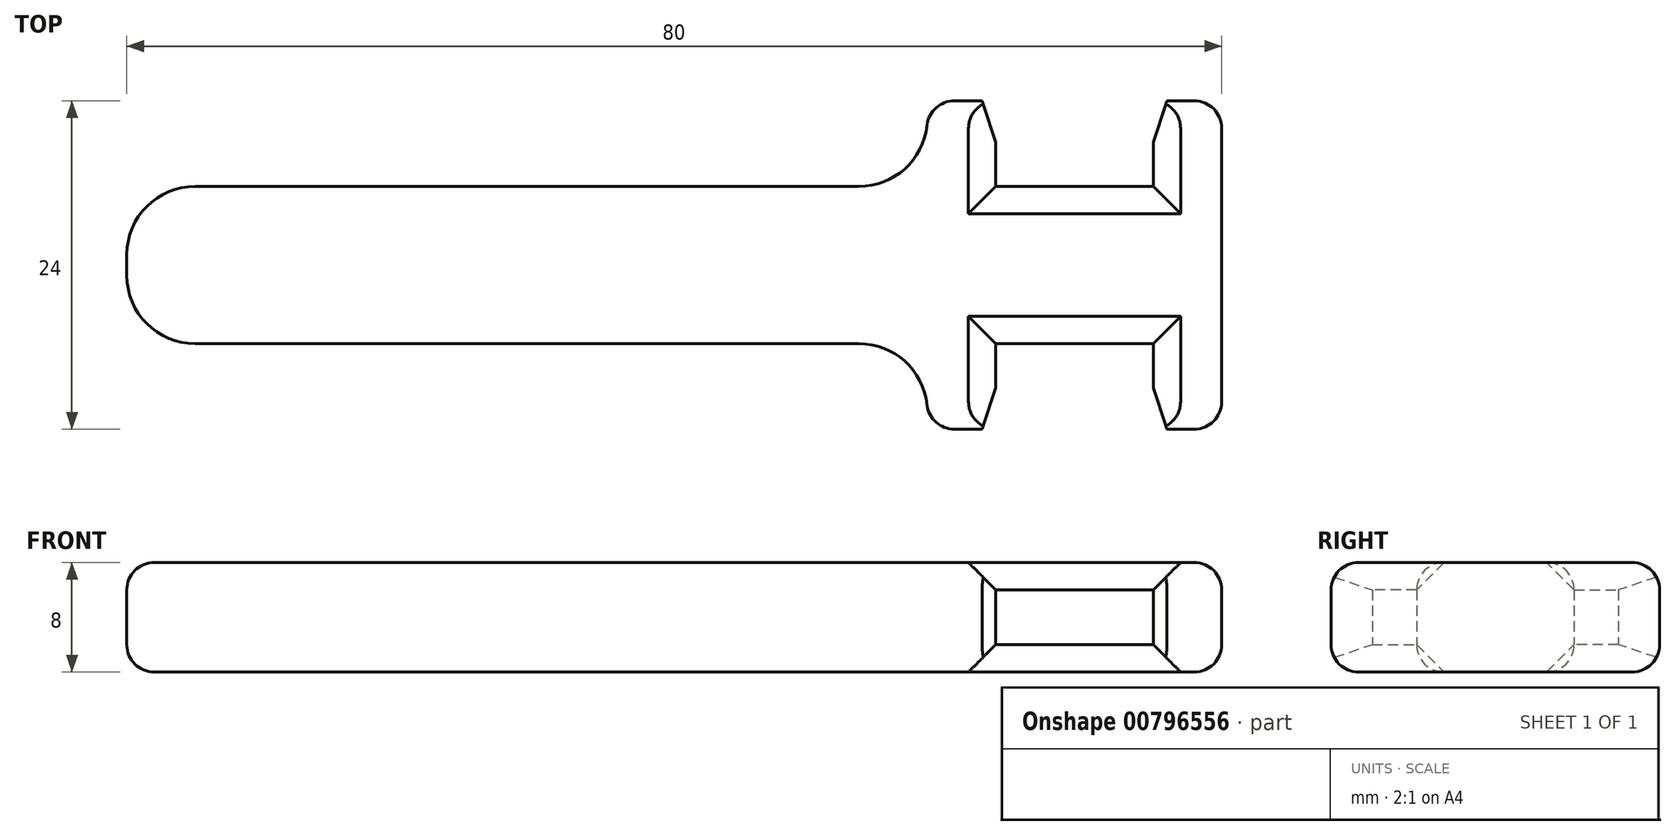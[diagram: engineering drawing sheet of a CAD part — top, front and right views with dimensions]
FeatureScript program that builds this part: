
annotation { "Feature Type Name" : "Feature", "Feature Type Description" : "" }
export const myFeature = defineFeature(function(context is Context, id is Id, definition is map)
    precondition{}
    {
        {
            var Q0;
            Q0=qCreatedBy(makeId("Top.planeOp"),FACE);
            var sketch = newSketch(context, id + "F0", { "sketchPlane" : qUnion([Q0])});
            skLineSegment(sketch, "E0.bottom", {"start": v(35, -5.75) * mm, "end": v(23.5, -5.75) * mm});
            skLineSegment(sketch, "E0.top", {"start": v(35, 5.75) * mm, "end": v(23.5, 5.75) * mm});
            skLineSegment(sketch, "E0.left", {"start": v(40, -5.75) * mm, "end": v(40, 5.75) * mm});
            skLineSegment(sketch, "E0.right", {"start": v(-40, -5.75) * mm, "end": v(-40, 5.75) * mm});
            skPoint(sketch, "E0.middle", {"position": v(0, 0) * mm});
            skLineSegment(sketch, "E1.bottom", {"start": v(40, 12) * mm, "end": v(35, 12) * mm});
            skLineSegment(sketch, "E1.top", {"start": v(40, -12) * mm, "end": v(35, -12) * mm});
            skLineSegment(sketch, "E1.left", {"start": v(40, 12) * mm, "end": v(40, -12) * mm});
            skLineSegment(sketch, "E1.right", {"start": v(35, 12) * mm, "end": v(35, 5.75) * mm});
            skLineSegment(sketch, "E2.trimOffspring", {"start": v(35, -5.75) * mm, "end": v(35, -12) * mm});
            skLineSegment(sketch, "E3.bottom", {"start": v(18.5, -12) * mm, "end": v(23.5, -12) * mm});
            skLineSegment(sketch, "E3.top", {"start": v(18.5, 12) * mm, "end": v(23.5, 12) * mm});
            skLineSegment(sketch, "E3.left", {"start": v(18.5, -12) * mm, "end": v(18.5, -5.75) * mm});
            skLineSegment(sketch, "E3.right", {"start": v(23.5, -12) * mm, "end": v(23.5, -5.75) * mm});
            skPoint(sketch, "E3.middle", {"position": v(21, 0) * mm});
            skLineSegment(sketch, "E4.trimOffspring", {"start": v(23.5, 5.75) * mm, "end": v(23.5, 12) * mm});
            skLineSegment(sketch, "E5.trimOffspring", {"start": v(18.5, 5.75) * mm, "end": v(18.5, 12) * mm});
            skLineSegment(sketch, "E6.trimOffspring", {"start": v(18.5, 5.75) * mm, "end": v(-40, 5.75) * mm});
            skLineSegment(sketch, "E7.trimOffspring", {"start": v(18.5, -5.75) * mm, "end": v(-40, -5.75) * mm});
            skSolve(sketch);
        }
        {
            var Q0;
            Q0 = qSketchRegion(id + "F0", true);
            extrude(context, id + "F1", {"entities" : qUnion([Q0]), "depth" : 8 * mm, "offsetDistance" : 25 * mm});
        }
        {
            var Q0;
            Q0=makeQuery(id+"F1.opExtrude","SWEPT_EDGE",EDGE,{"disambiguationData":[OSD([sQuery(id+"F0.wireOp",EDGE,"E3.left"),sQuery(id+"F0.wireOp",EDGE,"E7.trimOffspring")])]});
            var Q1;
            Q1=makeQuery(id+"F1.opExtrude","SWEPT_EDGE",EDGE,{"disambiguationData":[OSD([sQuery(id+"F0.wireOp",EDGE,"E5.trimOffspring"),sQuery(id+"F0.wireOp",EDGE,"E6.trimOffspring")])]});
            var Q2;
            Q2=makeQuery(id+"F1.opExtrude","SWEPT_EDGE",EDGE,{"disambiguationData":[OSD([sQuery(id+"F0.wireOp",EDGE,"E0.right"),sQuery(id+"F0.wireOp",EDGE,"E7.trimOffspring")])]});
            var Q3;
            Q3=makeQuery(id+"F1.opExtrude","SWEPT_EDGE",EDGE,{"disambiguationData":[OSD([sQuery(id+"F0.wireOp",EDGE,"E0.right"),sQuery(id+"F0.wireOp",EDGE,"E6.trimOffspring")])]});
            fillet(context, id + "F2", {"entities" : qUnion([Q0, Q1, Q2, Q3]), "radius" : 5 * mm, "tangentPropagation" : true, "allowEdgeOverflow" : false});
        }
        {
            var Q0;
            Q0=makeQuery(id+"F1.opExtrude","SWEPT_EDGE",EDGE,{"disambiguationData":[OSD([sQuery(id+"F0.wireOp",EDGE,"E1.top"),sQuery(id+"F0.wireOp",EDGE,"E1.left")])]});
            var Q1;
            Q1=makeQuery(id+"F1.opExtrude","SWEPT_EDGE",EDGE,{"disambiguationData":[OSD([sQuery(id+"F0.wireOp",EDGE,"E1.bottom"),sQuery(id+"F0.wireOp",EDGE,"E1.left")])]});
            var Q2;
            Q2=makeQuery(id+"F1.opExtrude","SWEPT_EDGE",EDGE,{"disambiguationData":[OSD([sQuery(id+"F0.wireOp",EDGE,"E3.bottom"),sQuery(id+"F0.wireOp",EDGE,"E3.left")])]});
            var Q3;
            Q3=makeQuery(id+"F1.opExtrude","SWEPT_EDGE",EDGE,{"disambiguationData":[OSD([sQuery(id+"F0.wireOp",EDGE,"E3.top"),sQuery(id+"F0.wireOp",EDGE,"E5.trimOffspring")])]});
            fillet(context, id + "F3", {"entities" : qUnion([Q0, Q1, Q2, Q3]), "radius" : 2 * mm, "tangentPropagation" : true, "allowEdgeOverflow" : false});
        }
        {
            var Q0;
            Q0=makeQuery(id+"F1.opExtrude","SWEPT_EDGE",EDGE,{"disambiguationData":[OSD([sQuery(id+"F0.wireOp",EDGE,"E3.top"),sQuery(id+"F0.wireOp",EDGE,"E4.trimOffspring")])]});
            var Q1;
            Q1=makeQuery(id+"F1.opExtrude","SWEPT_EDGE",EDGE,{"disambiguationData":[OSD([sQuery(id+"F0.wireOp",EDGE,"E1.top"),sQuery(id+"F0.wireOp",EDGE,"E2.trimOffspring")])]});
            chamfer(context, id + "F4", {"entities" : qUnion([Q0, Q1]), "chamferType" : ChamferType.TWO_OFFSETS, "width1" : 1 * mm, "oppositeDirection" : false, "width2" : 3 * mm, "tangentPropagation" : true});
        }
        {
            var Q0;
            Q0=makeQuery(id+"F1.opExtrude","SWEPT_EDGE",EDGE,{"disambiguationData":[OSD([sQuery(id+"F0.wireOp",EDGE,"E3.bottom"),sQuery(id+"F0.wireOp",EDGE,"E3.right")])]});
            var Q1;
            Q1=makeQuery(id+"F1.opExtrude","SWEPT_EDGE",EDGE,{"disambiguationData":[OSD([sQuery(id+"F0.wireOp",EDGE,"E1.bottom"),sQuery(id+"F0.wireOp",EDGE,"E1.right")])]});
            chamfer(context, id + "F5", {"entities" : qUnion([Q0, Q1]), "chamferType" : ChamferType.TWO_OFFSETS, "width1" : 3 * mm, "oppositeDirection" : false, "width2" : 1 * mm, "tangentPropagation" : true});
        }
        {
            var Q0;
            Q0=makeQuery(id+"F1.opExtrude","CAP_EDGE",EDGE,{"disambiguationData":[OSD([sQuery(id+"F0.wireOp",EDGE,"E0.top")])],"isStart":false});
            var Q1;
            Q1=makeQuery(id+"F1.opExtrude","CAP_EDGE",EDGE,{"disambiguationData":[OSD([sQuery(id+"F0.wireOp",EDGE,"E0.bottom")])],"isStart":false});
            var Q2;
            Q2=makeQuery(id+"F1.opExtrude","CAP_EDGE",EDGE,{"disambiguationData":[OSD([sQuery(id+"F0.wireOp",EDGE,"E0.bottom")])],"isStart":true});
            var Q3;
            Q3=makeQuery(id+"F1.opExtrude","CAP_EDGE",EDGE,{"disambiguationData":[OSD([sQuery(id+"F0.wireOp",EDGE,"E0.top")])],"isStart":true});
            var Q4;
            Q4=makeQuery(id+"F1.opExtrude","CAP_EDGE",EDGE,{"disambiguationData":[OSD([sQuery(id+"F0.wireOp",EDGE,"E4.trimOffspring")])],"isStart":true});
            var Q5;
            Q5=makeQuery(id+"F1.opExtrude","CAP_EDGE",EDGE,{"disambiguationData":[OSD([sQuery(id+"F0.wireOp",EDGE,"E4.trimOffspring")])],"isStart":false});
            var Q6;
            Q6=makeQuery(id+"F1.opExtrude","CAP_EDGE",EDGE,{"disambiguationData":[OSD([sQuery(id+"F0.wireOp",EDGE,"E3.right")])],"isStart":false});
            var Q7;
            Q7=makeQuery(id+"F1.opExtrude","CAP_EDGE",EDGE,{"disambiguationData":[OSD([sQuery(id+"F0.wireOp",EDGE,"E3.right")])],"isStart":true});
            var Q8;
            Q8=makeQuery(id+"F1.opExtrude","CAP_EDGE",EDGE,{"disambiguationData":[OSD([sQuery(id+"F0.wireOp",EDGE,"E2.trimOffspring")])],"isStart":true});
            var Q9;
            Q9=makeQuery(id+"F1.opExtrude","CAP_EDGE",EDGE,{"disambiguationData":[OSD([sQuery(id+"F0.wireOp",EDGE,"E2.trimOffspring")])],"isStart":false});
            var Q10;
            Q10=makeQuery(id+"F1.opExtrude","CAP_EDGE",EDGE,{"disambiguationData":[OSD([sQuery(id+"F0.wireOp",EDGE,"E1.right")])],"isStart":true});
            var Q11;
            Q11=makeQuery(id+"F1.opExtrude","CAP_EDGE",EDGE,{"disambiguationData":[OSD([sQuery(id+"F0.wireOp",EDGE,"E1.right")])],"isStart":false});
            chamfer(context, id + "F6", {"entities" : qUnion([Q0, Q1, Q2, Q3, Q4, Q5, Q6, Q7, Q8, Q9, Q10, Q11]), "width" : 2 * mm, "tangentPropagation" : true});
        }
        {
            var Q0;
            Q0=makeQuery(id+"F1.opExtrude","CAP_EDGE",EDGE,{"disambiguationData":[OSD([sQuery(id+"F0.wireOp",EDGE,"E7.trimOffspring")])],"isStart":true});
            fillet(context, id + "F7", {"entities" : qUnion([Q0]), "radius" : 2 * mm, "tangentPropagation" : true, "allowEdgeOverflow" : false});
        }
        {
            var Q0;
            Q0=makeQuery(id+"F1.opExtrude","CAP_EDGE",EDGE,{"disambiguationData":[OSD([sQuery(id+"F0.wireOp",EDGE,"E7.trimOffspring")])],"isStart":false});
            var Q1;
            {var subQ0=sQuery(id+"F0.wireOp",EDGE,"E7.trimOffspring");var subQ1=sQuery(id+"F0.wireOp",EDGE,"E3.left");Q1=makeQuery(id+"F2.opFillet","BLEND_EDGE",EDGE,{"blendedFrom":[makeQuery(id+"F1.opExtrude","SWEPT_EDGE",EDGE,{"disambiguationData":[OSD([subQ1,subQ0])]}),makeQuery(id+"F1.opExtrude","CAP_FACE",FACE,{"disambiguationData":[OSD([sQuery(id+"F0.wireOp",EDGE,"E0.bottom"),sQuery(id+"F0.wireOp",EDGE,"E0.top"),sQuery(id+"F0.wireOp",EDGE,"E0.right"),sQuery(id+"F0.wireOp",EDGE,"E1.bottom"),sQuery(id+"F0.wireOp",EDGE,"E1.top"),sQuery(id+"F0.wireOp",EDGE,"E1.left"),sQuery(id+"F0.wireOp",EDGE,"E1.right"),sQuery(id+"F0.wireOp",EDGE,"E2.trimOffspring"),sQuery(id+"F0.wireOp",EDGE,"E3.bottom"),sQuery(id+"F0.wireOp",EDGE,"E3.top"),subQ1,sQuery(id+"F0.wireOp",EDGE,"E3.right"),sQuery(id+"F0.wireOp",EDGE,"E4.trimOffspring"),sQuery(id+"F0.wireOp",EDGE,"E5.trimOffspring"),sQuery(id+"F0.wireOp",EDGE,"E6.trimOffspring"),subQ0])],"isStart":false})],"blendedInto":[makeQuery(id+"F1.opExtrude","CAP_FACE",FACE,{"disambiguationData":[OSD([sQuery(id+"F0.wireOp",EDGE,"E0.bottom"),sQuery(id+"F0.wireOp",EDGE,"E0.top"),sQuery(id+"F0.wireOp",EDGE,"E0.right"),sQuery(id+"F0.wireOp",EDGE,"E1.bottom"),sQuery(id+"F0.wireOp",EDGE,"E1.top"),sQuery(id+"F0.wireOp",EDGE,"E1.left"),sQuery(id+"F0.wireOp",EDGE,"E1.right"),sQuery(id+"F0.wireOp",EDGE,"E2.trimOffspring"),sQuery(id+"F0.wireOp",EDGE,"E3.bottom"),sQuery(id+"F0.wireOp",EDGE,"E3.top"),subQ1,sQuery(id+"F0.wireOp",EDGE,"E3.right"),sQuery(id+"F0.wireOp",EDGE,"E4.trimOffspring"),sQuery(id+"F0.wireOp",EDGE,"E5.trimOffspring"),sQuery(id+"F0.wireOp",EDGE,"E6.trimOffspring"),subQ0])],"isStart":false})]});}
            var Q2;
            Q2=makeQuery(id+"F1.opExtrude","CAP_EDGE",EDGE,{"disambiguationData":[OSD([sQuery(id+"F0.wireOp",EDGE,"E6.trimOffspring")])],"isStart":false});
            var Q3;
            {var subQ0=sQuery(id+"F0.wireOp",EDGE,"E6.trimOffspring");var subQ1=sQuery(id+"F0.wireOp",EDGE,"E5.trimOffspring");Q3=makeQuery(id+"F2.opFillet","BLEND_EDGE",EDGE,{"blendedFrom":[makeQuery(id+"F1.opExtrude","SWEPT_EDGE",EDGE,{"disambiguationData":[OSD([subQ1,subQ0])]}),makeQuery(id+"F1.opExtrude","CAP_FACE",FACE,{"disambiguationData":[OSD([sQuery(id+"F0.wireOp",EDGE,"E0.bottom"),sQuery(id+"F0.wireOp",EDGE,"E0.top"),sQuery(id+"F0.wireOp",EDGE,"E0.right"),sQuery(id+"F0.wireOp",EDGE,"E1.bottom"),sQuery(id+"F0.wireOp",EDGE,"E1.top"),sQuery(id+"F0.wireOp",EDGE,"E1.left"),sQuery(id+"F0.wireOp",EDGE,"E1.right"),sQuery(id+"F0.wireOp",EDGE,"E2.trimOffspring"),sQuery(id+"F0.wireOp",EDGE,"E3.bottom"),sQuery(id+"F0.wireOp",EDGE,"E3.top"),sQuery(id+"F0.wireOp",EDGE,"E3.left"),sQuery(id+"F0.wireOp",EDGE,"E3.right"),sQuery(id+"F0.wireOp",EDGE,"E4.trimOffspring"),subQ1,subQ0,sQuery(id+"F0.wireOp",EDGE,"E7.trimOffspring")])],"isStart":false})],"blendedInto":[makeQuery(id+"F1.opExtrude","CAP_FACE",FACE,{"disambiguationData":[OSD([sQuery(id+"F0.wireOp",EDGE,"E0.bottom"),sQuery(id+"F0.wireOp",EDGE,"E0.top"),sQuery(id+"F0.wireOp",EDGE,"E0.right"),sQuery(id+"F0.wireOp",EDGE,"E1.bottom"),sQuery(id+"F0.wireOp",EDGE,"E1.top"),sQuery(id+"F0.wireOp",EDGE,"E1.left"),sQuery(id+"F0.wireOp",EDGE,"E1.right"),sQuery(id+"F0.wireOp",EDGE,"E2.trimOffspring"),sQuery(id+"F0.wireOp",EDGE,"E3.bottom"),sQuery(id+"F0.wireOp",EDGE,"E3.top"),sQuery(id+"F0.wireOp",EDGE,"E3.left"),sQuery(id+"F0.wireOp",EDGE,"E3.right"),sQuery(id+"F0.wireOp",EDGE,"E4.trimOffspring"),subQ1,subQ0,sQuery(id+"F0.wireOp",EDGE,"E7.trimOffspring")])],"isStart":false})]});}
            var Q4;
            {var subQ0=sQuery(id+"F0.wireOp",EDGE,"E7.trimOffspring");var subQ1=sQuery(id+"F0.wireOp",EDGE,"E0.right");Q4=makeQuery(id+"F2.opFillet","BLEND_EDGE",EDGE,{"blendedFrom":[makeQuery(id+"F1.opExtrude","SWEPT_EDGE",EDGE,{"disambiguationData":[OSD([subQ1,subQ0])]}),makeQuery(id+"F1.opExtrude","CAP_FACE",FACE,{"disambiguationData":[OSD([sQuery(id+"F0.wireOp",EDGE,"E0.bottom"),sQuery(id+"F0.wireOp",EDGE,"E0.top"),subQ1,sQuery(id+"F0.wireOp",EDGE,"E1.bottom"),sQuery(id+"F0.wireOp",EDGE,"E1.top"),sQuery(id+"F0.wireOp",EDGE,"E1.left"),sQuery(id+"F0.wireOp",EDGE,"E1.right"),sQuery(id+"F0.wireOp",EDGE,"E2.trimOffspring"),sQuery(id+"F0.wireOp",EDGE,"E3.bottom"),sQuery(id+"F0.wireOp",EDGE,"E3.top"),sQuery(id+"F0.wireOp",EDGE,"E3.left"),sQuery(id+"F0.wireOp",EDGE,"E3.right"),sQuery(id+"F0.wireOp",EDGE,"E4.trimOffspring"),sQuery(id+"F0.wireOp",EDGE,"E5.trimOffspring"),sQuery(id+"F0.wireOp",EDGE,"E6.trimOffspring"),subQ0])],"isStart":false})],"blendedInto":[makeQuery(id+"F1.opExtrude","CAP_FACE",FACE,{"disambiguationData":[OSD([sQuery(id+"F0.wireOp",EDGE,"E0.bottom"),sQuery(id+"F0.wireOp",EDGE,"E0.top"),subQ1,sQuery(id+"F0.wireOp",EDGE,"E1.bottom"),sQuery(id+"F0.wireOp",EDGE,"E1.top"),sQuery(id+"F0.wireOp",EDGE,"E1.left"),sQuery(id+"F0.wireOp",EDGE,"E1.right"),sQuery(id+"F0.wireOp",EDGE,"E2.trimOffspring"),sQuery(id+"F0.wireOp",EDGE,"E3.bottom"),sQuery(id+"F0.wireOp",EDGE,"E3.top"),sQuery(id+"F0.wireOp",EDGE,"E3.left"),sQuery(id+"F0.wireOp",EDGE,"E3.right"),sQuery(id+"F0.wireOp",EDGE,"E4.trimOffspring"),sQuery(id+"F0.wireOp",EDGE,"E5.trimOffspring"),sQuery(id+"F0.wireOp",EDGE,"E6.trimOffspring"),subQ0])],"isStart":false})]});}
            var Q5;
            {var subQ0=sQuery(id+"F0.wireOp",EDGE,"E6.trimOffspring");var subQ1=sQuery(id+"F0.wireOp",EDGE,"E0.right");Q5=makeQuery(id+"F2.opFillet","BLEND_EDGE",EDGE,{"blendedFrom":[makeQuery(id+"F1.opExtrude","SWEPT_EDGE",EDGE,{"disambiguationData":[OSD([subQ1,subQ0])]}),makeQuery(id+"F1.opExtrude","CAP_FACE",FACE,{"disambiguationData":[OSD([sQuery(id+"F0.wireOp",EDGE,"E0.bottom"),sQuery(id+"F0.wireOp",EDGE,"E0.top"),subQ1,sQuery(id+"F0.wireOp",EDGE,"E1.bottom"),sQuery(id+"F0.wireOp",EDGE,"E1.top"),sQuery(id+"F0.wireOp",EDGE,"E1.left"),sQuery(id+"F0.wireOp",EDGE,"E1.right"),sQuery(id+"F0.wireOp",EDGE,"E2.trimOffspring"),sQuery(id+"F0.wireOp",EDGE,"E3.bottom"),sQuery(id+"F0.wireOp",EDGE,"E3.top"),sQuery(id+"F0.wireOp",EDGE,"E3.left"),sQuery(id+"F0.wireOp",EDGE,"E3.right"),sQuery(id+"F0.wireOp",EDGE,"E4.trimOffspring"),sQuery(id+"F0.wireOp",EDGE,"E5.trimOffspring"),subQ0,sQuery(id+"F0.wireOp",EDGE,"E7.trimOffspring")])],"isStart":false})],"blendedInto":[makeQuery(id+"F1.opExtrude","CAP_FACE",FACE,{"disambiguationData":[OSD([sQuery(id+"F0.wireOp",EDGE,"E0.bottom"),sQuery(id+"F0.wireOp",EDGE,"E0.top"),subQ1,sQuery(id+"F0.wireOp",EDGE,"E1.bottom"),sQuery(id+"F0.wireOp",EDGE,"E1.top"),sQuery(id+"F0.wireOp",EDGE,"E1.left"),sQuery(id+"F0.wireOp",EDGE,"E1.right"),sQuery(id+"F0.wireOp",EDGE,"E2.trimOffspring"),sQuery(id+"F0.wireOp",EDGE,"E3.bottom"),sQuery(id+"F0.wireOp",EDGE,"E3.top"),sQuery(id+"F0.wireOp",EDGE,"E3.left"),sQuery(id+"F0.wireOp",EDGE,"E3.right"),sQuery(id+"F0.wireOp",EDGE,"E4.trimOffspring"),sQuery(id+"F0.wireOp",EDGE,"E5.trimOffspring"),subQ0,sQuery(id+"F0.wireOp",EDGE,"E7.trimOffspring")])],"isStart":false})]});}
            var Q6;
            Q6=makeQuery(id+"F1.opExtrude","CAP_EDGE",EDGE,{"disambiguationData":[OSD([sQuery(id+"F0.wireOp",EDGE,"E1.left")])],"isStart":false});
            var Q7;
            Q7=makeQuery(id+"F1.opExtrude","CAP_EDGE",EDGE,{"disambiguationData":[OSD([sQuery(id+"F0.wireOp",EDGE,"E1.left")])],"isStart":true});
            fillet(context, id + "F8", {"entities" : qUnion([Q0, Q1, Q2, Q3, Q4, Q5, Q6, Q7]), "radius" : 2 * mm, "tangentPropagation" : true, "allowEdgeOverflow" : false});
        }
    });
